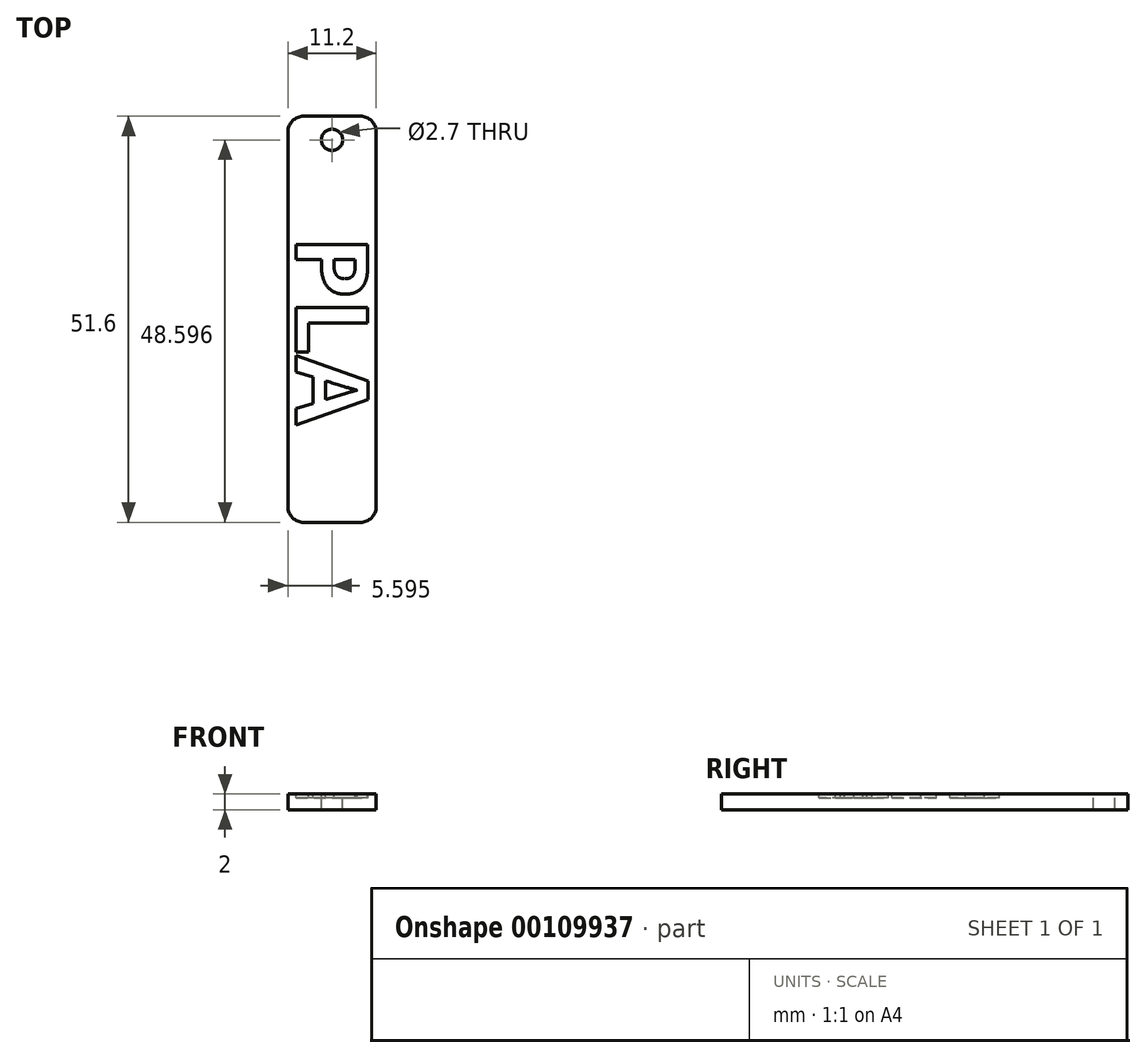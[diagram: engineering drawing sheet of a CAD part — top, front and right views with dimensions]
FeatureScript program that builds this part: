
annotation { "Feature Type Name" : "Feature", "Feature Type Description" : "" }
export const myFeature = defineFeature(function(context is Context, id is Id, definition is map)
    precondition{}
    {
        {
            var Q0;
            Q0=qCreatedBy(makeId("Top.planeOp"),FACE);
            var sketch = newSketch(context, id + "F0", { "sketchPlane" : qUnion([Q0])});
            skLineSegment(sketch, "E0.bottom", {"start": v(-49.26, 80.3) * mm, "end": v(-38.06, 80.3) * mm});
            skLineSegment(sketch, "E0.top", {"start": v(-49.26, 28.7) * mm, "end": v(-38.06, 28.7) * mm});
            skLineSegment(sketch, "E0.left", {"start": v(-49.26, 80.3) * mm, "end": v(-49.26, 28.7) * mm});
            skLineSegment(sketch, "E0.right", {"start": v(-38.06, 80.3) * mm, "end": v(-38.06, 28.7) * mm});
            skCircle(sketch, "E1", {"center": v(-43.66, 77.3) * mm, "radius": 1.35 * mm});
            skText(sketch, "E2", { "text": "PLA", "fontName": "OpenSans-Bold.ttf"});
            const initialGuessF0  = {"E2": [-0.04826, 0.06514, 0, -1, 0.0092]};
            skSetInitialGuess(sketch, initialGuessF0);
            skSolve(sketch);
        }
        {
            var Q0;
            Q0 = qSketchRegion(id + "F0", true);
            var Q1;
            Q1=makeQuery(id+"F0.imprint","IMPRINT",FACE,{"disambiguationData":[TD([[makeQuery(id+"F0.imprint","IMPRINT",EDGE,{"derivedFrom":sQuery(id+"F0.wireOp",EDGE,"E2.sketch_text.stroke-0")}),-1.0]])]});
            var Q2;
            Q2=makeQuery(id+"F0.imprint","IMPRINT",FACE,{"disambiguationData":[TD([[makeQuery(id+"F0.imprint","IMPRINT",EDGE,{"derivedFrom":sQuery(id+"F0.wireOp",EDGE,"E2.sketch_text.stroke-8")}),1.0]])]});
            var Q3;
            Q3=makeQuery(id+"F0.imprint","IMPRINT",FACE,{"disambiguationData":[TD([[makeQuery(id+"F0.imprint","IMPRINT",EDGE,{"derivedFrom":sQuery(id+"F0.wireOp",EDGE,"E2.sketch_text.stroke-15")}),-1.0]])]});
            var Q4;
            Q4=makeQuery(id+"F0.imprint","IMPRINT",FACE,{"disambiguationData":[TD([[makeQuery(id+"F0.imprint","IMPRINT",EDGE,{"derivedFrom":sQuery(id+"F0.wireOp",EDGE,"E2.sketch_text.stroke-29")}),1.0]])]});
            var Q5;
            Q5=makeQuery(id+"F0.imprint","IMPRINT",FACE,{"disambiguationData":[TD([[makeQuery(id+"F0.imprint","IMPRINT",EDGE,{"derivedFrom":sQuery(id+"F0.wireOp",EDGE,"E2.sketch_text.stroke-21")}),-1.0]])]});
            var Q6;
            Q6=makeQuery(id+"F0.imprint","IMPRINT",FACE,{"disambiguationData":[TD([[makeQuery(id+"F0.imprint","IMPRINT",EDGE,{"derivedFrom":sQuery(id+"F0.wireOp",EDGE,"E2.sketch_text.stroke-0")}),1.0]])]});
            var Q7;
            Q7=makeQuery(id+"F0.imprint","IMPRINT",FACE,{"disambiguationData":[TD([[makeQuery(id+"F0.imprint","IMPRINT",EDGE,{"derivedFrom":sQuery(id+"F0.wireOp",EDGE,"E2.sketch_text.stroke-22")}),-1.0]])]});
            var Q8;
            Q8=makeQuery(id+"F0.imprint","IMPRINT",FACE,{"disambiguationData":[TD([[makeQuery(id+"F0.imprint","IMPRINT",EDGE,{"derivedFrom":sQuery(id+"F0.wireOp",EDGE,"E2.sketch_text.stroke-30")}),1.0]])]});
            extrude(context, id + "F1", {"entities" : qUnion([Q0, Q1, Q2, Q3, Q4, Q5, Q6, Q7, Q8]), "oppositeDirection" : true, "depth" : 2 * mm});
        }
        {
            var Q0;
            Q0=makeQuery(id+"F0.imprint","IMPRINT",FACE,{"disambiguationData":[TD([[makeQuery(id+"F0.imprint","IMPRINT",EDGE,{"derivedFrom":sQuery(id+"F0.wireOp",EDGE,"E2.sketch_text.stroke-0")}),-1.0]])]});
            var Q1;
            Q1=makeQuery(id+"F0.imprint","IMPRINT",FACE,{"disambiguationData":[TD([[makeQuery(id+"F0.imprint","IMPRINT",EDGE,{"derivedFrom":sQuery(id+"F0.wireOp",EDGE,"E2.sketch_text.stroke-23")}),-1.0]])]});
            var Q2;
            Q2=makeQuery(id+"F0.imprint","IMPRINT",FACE,{"disambiguationData":[TD([[makeQuery(id+"F0.imprint","IMPRINT",EDGE,{"derivedFrom":sQuery(id+"F0.wireOp",EDGE,"E2.sketch_text.stroke-39")}),-1.0]])]});
            var Q3;
            Q3=makeQuery(id+"F0.imprint","IMPRINT",FACE,{"disambiguationData":[TD([[makeQuery(id+"F0.imprint","IMPRINT",EDGE,{"derivedFrom":sQuery(id+"F0.wireOp",EDGE,"E2.sketch_text.stroke-15")}),-1.0]])]});
            var Q4;
            Q4=makeQuery(id+"F0.imprint","IMPRINT",FACE,{"disambiguationData":[TD([[makeQuery(id+"F0.imprint","IMPRINT",EDGE,{"derivedFrom":sQuery(id+"F0.wireOp",EDGE,"E2.sketch_text.stroke-16")}),-1.0]])]});
            var Q5;
            Q5 = qConstructionFilter(qBodyType(qCreatedBy(id + "F0" ,EDGE), BodyType.WIRE), ConstructionObject.NO);
            extrude(context, id + "F2", {"entities" : qUnion([Q0, Q1, Q2, Q3, Q4]), "operationType" : NewBodyOperationType.REMOVE, "surfaceEntities" : qUnion([Q5]), "oppositeDirection" : true, "depth" : .5 * mm});
        }
        {
            var Q0;
            Q0=makeQuery(id+"F1.opExtrude","SWEPT_EDGE",EDGE,{"disambiguationData":[OSD([sQuery(id+"F0.wireOp",EDGE,"E0.bottom"),sQuery(id+"F0.wireOp",EDGE,"E0.left")])]});
            var Q1;
            Q1=makeQuery(id+"F1.opExtrude","SWEPT_EDGE",EDGE,{"disambiguationData":[OSD([sQuery(id+"F0.wireOp",EDGE,"E0.bottom"),sQuery(id+"F0.wireOp",EDGE,"E0.right")])]});
            var Q2;
            Q2=makeQuery(id+"F1.opExtrude","SWEPT_EDGE",EDGE,{"disambiguationData":[OSD([sQuery(id+"F0.wireOp",EDGE,"E0.top"),sQuery(id+"F0.wireOp",EDGE,"E0.right")])]});
            var Q3;
            Q3=makeQuery(id+"F1.opExtrude","SWEPT_EDGE",EDGE,{"disambiguationData":[OSD([sQuery(id+"F0.wireOp",EDGE,"E0.top"),sQuery(id+"F0.wireOp",EDGE,"E0.left")])]});
            fillet(context, id + "F3", {"entities" : qUnion([Q0, Q1, Q2, Q3]), "radius" : 2 * mm, "tangentPropagation" : true, "allowEdgeOverflow" : false});
        }
    });
